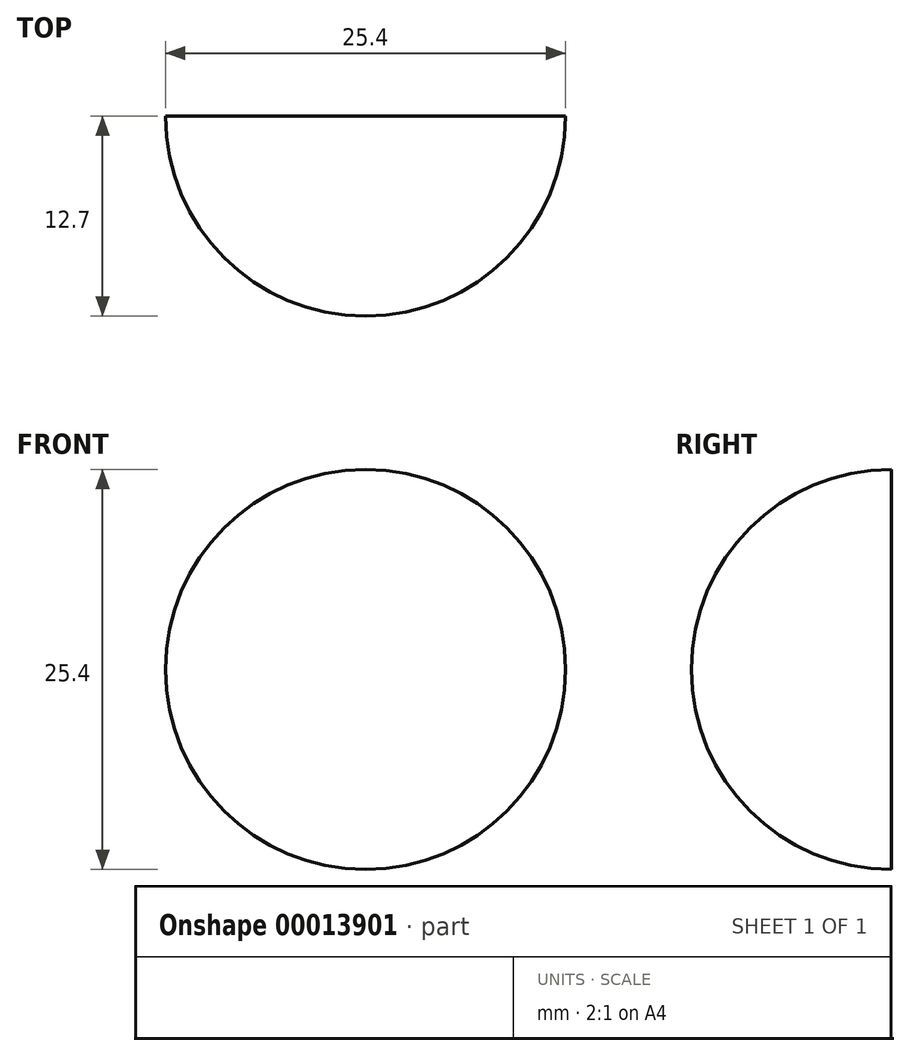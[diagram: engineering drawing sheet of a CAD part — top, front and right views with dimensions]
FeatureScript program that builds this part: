
annotation { "Feature Type Name" : "Feature", "Feature Type Description" : "" }
export const myFeature = defineFeature(function(context is Context, id is Id, definition is map)
    precondition{}
    {
        {
            var Q0;
            Q0=qCreatedBy(makeId("Front.planeOp"),FACE);
            var sketch = newSketch(context, id + "F0", { "sketchPlane" : qUnion([Q0])});
            skArc(sketch, "E0", {"start": v(0, 12.7) * mm, "mid": v(-12.7, 0) * mm, "end": v(0, -12.7) * mm});
            skLineSegment(sketch, "E1", {"start": v(0, 0) * mm, "end": v(0, -12.7) * mm});
            skLineSegment(sketch, "E2", {"start": v(0, 0) * mm, "end": v(0, 12.7) * mm});
            skSolve(sketch);
        }
        {
            var Q0;
            Q0=makeQuery(id+"F0.imprint","IMPRINT",FACE,{"disambiguationData":[TD([[makeQuery(id+"F0.imprint","IMPRINT",EDGE,{"derivedFrom":sQuery(id+"F0.wireOp",EDGE,"E0")}),1.0]])]});
            var Q1;
            Q1=sQuery(id+"F0.wireOp",EDGE,"E2");
            revolve(context, id + "F1", {"entities" : qUnion([Q0]), "axis" : qUnion([Q1]), "revolveType" : RevolveType.FULL});
        }
        {
            var Q0;
            Q0=qCreatedBy(makeId("Front.planeOp"),FACE);
            var sketch = newSketch(context, id + "F2", { "sketchPlane" : qUnion([Q0])});
            skLineSegment(sketch, "E3.bottom", {"start": v(-32.14, 32.14) * mm, "end": v(32.14, 32.14) * mm});
            skLineSegment(sketch, "E3.top", {"start": v(-32.14, -32.14) * mm, "end": v(32.14, -32.14) * mm});
            skLineSegment(sketch, "E3.left", {"start": v(-32.14, 32.14) * mm, "end": v(-32.14, -32.14) * mm});
            skLineSegment(sketch, "E3.right", {"start": v(32.14, 32.14) * mm, "end": v(32.14, -32.14) * mm});
            skLineSegment(sketch, "E4", {"start": v(0, 32.14) * mm, "end": v(0, 0) * mm, "construction": true});
            skLineSegment(sketch, "E5", {"start": v(0, 0) * mm, "end": v(0, -32.14) * mm, "construction": true});
            skLineSegment(sketch, "E6", {"start": v(-32.14, 0) * mm, "end": v(0, 0) * mm});
            skLineSegment(sketch, "E7", {"start": v(0, 0) * mm, "end": v(32.14, 0) * mm, "construction": true});
            skSolve(sketch);
        }
        {
            var Q0;
            Q0 = qSketchRegion(id + "F2", true);
            extrude(context, id + "F3", {"entities" : qUnion([Q0]), "operationType" : NewBodyOperationType.REMOVE, "oppositeDirection" : true, "depth" : 12.7 * mm});
        }
    });
